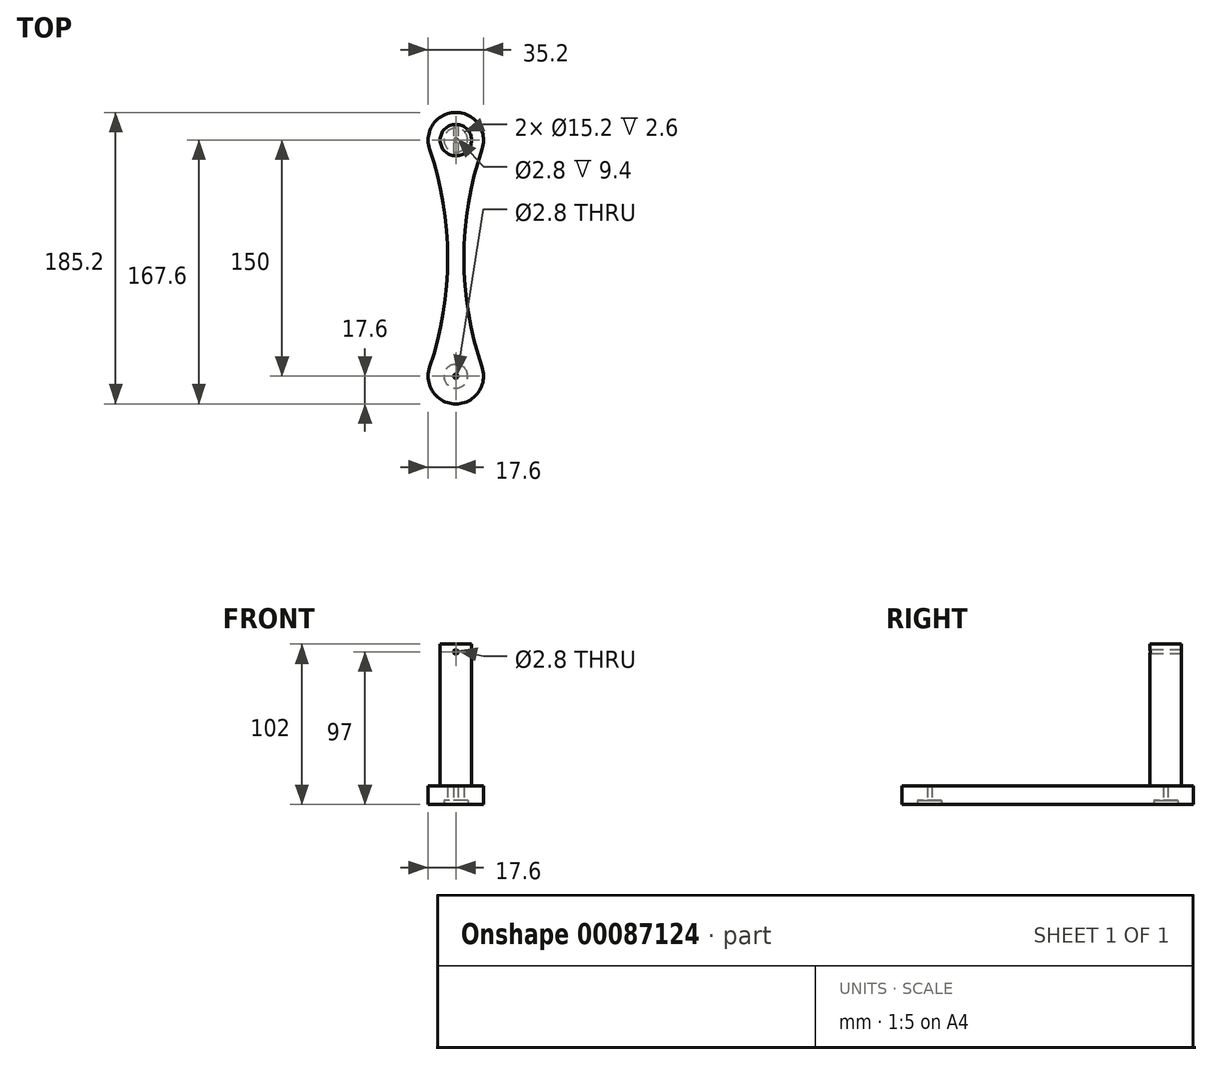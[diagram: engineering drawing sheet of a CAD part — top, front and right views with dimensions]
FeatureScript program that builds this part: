
annotation { "Feature Type Name" : "Feature", "Feature Type Description" : "" }
export const myFeature = defineFeature(function(context is Context, id is Id, definition is map)
    precondition{}
    {
        {
            var Q0;
            Q0=qCreatedBy(makeId("Top.planeOp"),FACE);
            var sketch = newSketch(context, id + "F0", { "sketchPlane" : qUnion([Q0])});
            skCircle(sketch, "E0", {"center": v(0, 0) * mm, "radius": 7.6 * mm});
            skCircle(sketch, "E1", {"center": v(0, 0) * mm, "radius": 17.6 * mm});
            skCircle(sketch, "E2", {"center": v(0, -150) * mm, "radius": 17.6 * mm});
            skLineSegment(sketch, "E3", {"start": v(0, 44.54) * mm, "end": v(0, -26.23) * mm, "construction": true});
            skArc(sketch, "E4", {"start": v(-16.65, -144.3) * mm, "mid": v(-5.12, -75) * mm, "end": v(-16.65, -5.7) * mm});
            skArc(sketch, "E5.MirrorCS", {"start": v(16.65, -144.3) * mm, "mid": v(5.12, -75) * mm, "end": v(16.65, -5.7) * mm});
            skSolve(sketch);
        }
        {
            var Q0;
            Q0 = qSketchRegion(id + "F0", true);
            var Q1;
            Q1=makeQuery(id+"F0.imprint","IMPRINT",FACE,{"disambiguationData":[TD([[makeQuery(id+"F0.imprint","IMPRINT",EDGE,{"derivedFrom":sQuery(id+"F0.wireOp",EDGE,"E0")}),1.0]])]});
            extrude(context, id + "F1", {"entities" : qUnion([Q0, Q1]), "depth" : 12 * mm});
        }
        {
            var Q0;
            Q0=qCreatedBy(makeId("Top.planeOp"),FACE);
            var sketch = newSketch(context, id + "F2", { "sketchPlane" : qUnion([Q0])});
            skCircle(sketch, "E6", {"center": v(0, 0) * mm, "radius": 7.6 * mm});
            skArc(sketch, "E7.0", {"start": v(-16.65, -144.3) * mm, "mid": v(0, -167.6) * mm, "end": v(16.65, -144.3) * mm, "construction": true});
            skCircle(sketch, "E8", {"center": v(0, -150) * mm, "radius": 7.6 * mm});
            skSolve(sketch);
        }
        {
            var Q0;
            Q0 = qSketchRegion(id + "F2", true);
            extrude(context, id + "F3", {"entities" : qUnion([Q0]), "operationType" : NewBodyOperationType.REMOVE, "depth" : 2.6 * mm});
        }
        {
            var Q0;
            Q0=qCreatedBy(makeId("Top.planeOp"),FACE);
            var sketch = newSketch(context, id + "F4", { "sketchPlane" : qUnion([Q0])});
            skCircle(sketch, "E9", {"center": v(0, 0) * mm, "radius": 1.4 * mm});
            skCircle(sketch, "E10.0", {"center": v(0, -150) * mm, "radius": 7.6 * mm, "construction": true});
            skCircle(sketch, "E11", {"center": v(0, -150) * mm, "radius": 1.4 * mm});
            skSolve(sketch);
        }
        {
            var Q0;
            Q0=makeQuery(id+"F4.imprint","IMPRINT",FACE,{"disambiguationData":[TD([[makeQuery(id+"F4.imprint","IMPRINT",EDGE,{"derivedFrom":sQuery(id+"F4.wireOp",EDGE,"E11")}),1.0]])]});
            var Q1;
            Q1=makeQuery(id+"F4.imprint","IMPRINT",FACE,{"disambiguationData":[TD([[makeQuery(id+"F4.imprint","IMPRINT",EDGE,{"derivedFrom":sQuery(id+"F4.wireOp",EDGE,"E9")}),1.0]])]});
            extrude(context, id + "F5", {"entities" : qUnion([Q0, Q1]), "operationType" : NewBodyOperationType.REMOVE, "endBound" : BoundingType.THROUGH_ALL, "depth" : 25 * mm});
        }
        {
            var Q0;
            Q0=makeQuery(id+"F1.opExtrude","CAP_FACE",FACE,{"disambiguationData":[OSD([sQuery(id+"F0.wireOp",EDGE,"E1"),sQuery(id+"F0.wireOp",EDGE,"E2"),sQuery(id+"F0.wireOp",EDGE,"E4"),sQuery(id+"F0.wireOp",EDGE,"E5.MirrorCS")])],"isStart":false});
            var sketch = newSketch(context, id + "F6", { "sketchPlane" : qUnion([Q0])});
            skCircle(sketch, "E12", {"center": v(0, 0) * mm, "radius": 10 * mm});
            skSolve(sketch);
        }
        {
            var Q0;
            Q0 = qSketchRegion(id + "F6", true);
            extrude(context, id + "F7", {"entities" : qUnion([Q0]), "operationType" : NewBodyOperationType.ADD, "depth" : 90 * mm});
        }
        {
            var Q0;
            Q0=qCreatedBy(makeId("Front.planeOp"),FACE);
            var sketch = newSketch(context, id + "F8", { "sketchPlane" : qUnion([Q0])});
            skCircle(sketch, "E13", {"center": v(0, 97) * mm, "radius": 1.4 * mm});
            skSolve(sketch);
        }
        {
            var Q0;
            Q0 = qSketchRegion(id + "F8", true);
            var Q1;
            Q1=sQuery(id+"F8.wireOp",EDGE,"E13");
            extrude(context, id + "F9", {"entities" : qUnion([Q0]), "operationType" : NewBodyOperationType.REMOVE, "surfaceEntities" : qUnion([Q1]), "endBound" : BoundingType.THROUGH_ALL, "oppositeDirection" : true, "depth" : 25 * mm, "hasSecondDirection" : true, "secondDirectionBound" : SecondDirectionBoundingType.THROUGH_ALL, "secondDirectionOppositeDirection" : false, "secondDirectionDepth" : 25 * mm});
        }
    });
